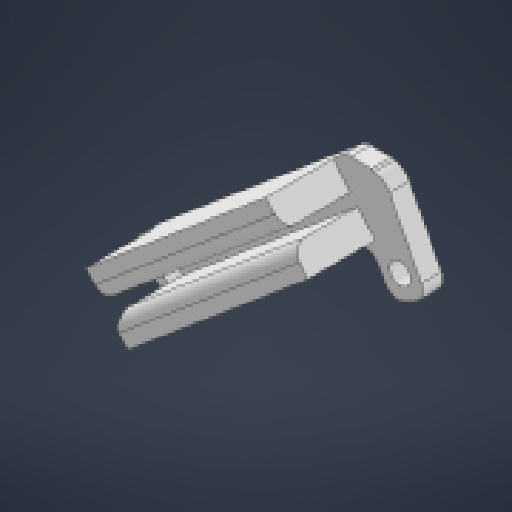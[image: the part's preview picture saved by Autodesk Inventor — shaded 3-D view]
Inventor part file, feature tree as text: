
AUTODESK INVENTOR PART (.ipt)
format: ipt  version: 2025 (Build 290162000, 162)  size: 274,944 bytes
history: native  units: mm
features: fillet x4, other x3, extrude x2, sketch x2, reference x1
ambient origin geometry x8: Origin, YZ Plane, XZ Plane, XY Plane, X Axis, Y Axis, Z Axis, Center Point
bodies: Solid1 (feature_tree)
feature tree (12):
  extrude  "Extrusion1"  Depth=2.0mm
  fillet  "Fillet1"  Radius=35.0mm
  extrude  "Extrusion2"  Depth=2.0mm
  fillet  "Fillet2"  Radius=4.0mm
  fillet  "Fillet3"  Radius=4.0mm
  fillet  "Fillet4"  Radius=10.0mm
  sketch  "Sketch1"  dims[d0=3.0mm d1=0.0mm d2=2.0mm d3=35.0mm]
  reference  "Reference1"
  sketch  "Sketch2"  dims[d4=6.981317mm d5=1.7mm d6=4.0mm d7=4.0mm d8=10.0mm d9=0.0mm d10=2.0mm d11=3.2mm d12=2.0mm d13=2.0mm]
  other  "<userpath> 7 was better\GitHub\ReplicatorPlusConversion\CAD\Inventor\Electronics.iam"
  other  "Electronics.iam"
  other  "skr-mini-mount:1"
